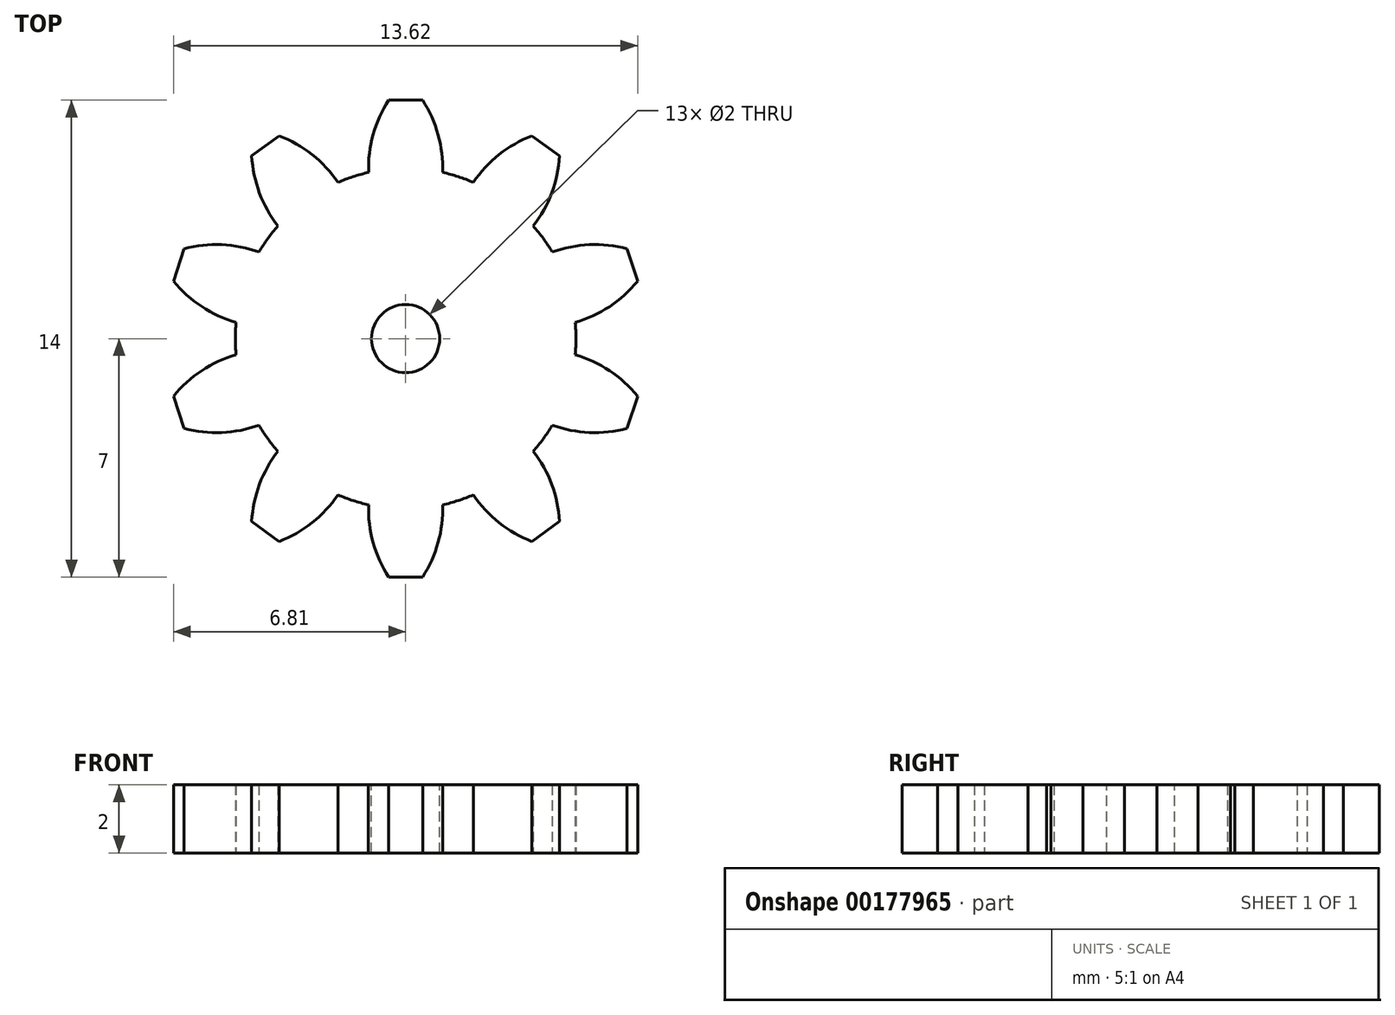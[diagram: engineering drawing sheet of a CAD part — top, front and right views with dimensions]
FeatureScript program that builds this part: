
annotation { "Feature Type Name" : "Feature", "Feature Type Description" : "" }
export const myFeature = defineFeature(function(context is Context, id is Id, definition is map)
    precondition{}
    {
        {
            var Q0;
            Q0=qCreatedBy(makeId("Top.planeOp"),FACE);
            var sketch = newSketch(context, id + "F0", { "sketchPlane" : qUnion([Q0])});
            skCircle(sketch, "E0", {"center": v(0, 0) * mm, "radius": 5 * mm});
            skLineSegment(sketch, "E1", {"start": v(0, 0) * mm, "end": v(0, 5) * mm, "construction": true});
            skLineSegment(sketch, "E2", {"start": v(0, 7) * mm, "end": v(-0.5, 7) * mm});
            skArc(sketch, "E3", {"start": v(-0.5, 7) * mm, "mid": v(-0.96, 5.98) * mm, "end": v(-1.09, 4.88) * mm});
            skLineSegment(sketch, "E4", {"start": v(0, 5) * mm, "end": v(0, 8.52) * mm});
            skLineSegment(sketch, "E5.MirrorCS", {"start": v(0, 7) * mm, "end": v(0.5, 7) * mm});
            skArc(sketch, "E6.MirrorCS", {"start": v(0.5, 7) * mm, "mid": v(0.96, 5.98) * mm, "end": v(1.09, 4.88) * mm});
            skArc(sketch, "E7.1.0", {"start": v(-4.52, 5.37) * mm, "mid": v(-4.3, 4.28) * mm, "end": v(-3.75, 3.3) * mm});
            skLineSegment(sketch, "E7.1.1", {"start": v(-4.11, 5.66) * mm, "end": v(-4.52, 5.37) * mm});
            skLineSegment(sketch, "E7.1.2", {"start": v(-4.11, 5.66) * mm, "end": v(-3.7, 5.96) * mm});
            skArc(sketch, "E7.1.3", {"start": v(-3.7, 5.96) * mm, "mid": v(-2.75, 5.4) * mm, "end": v(-1.99, 4.59) * mm});
            skArc(sketch, "E7.2.0", {"start": v(-6.81, 1.69) * mm, "mid": v(-5.99, 0.94) * mm, "end": v(-4.98, 0.47) * mm});
            skLineSegment(sketch, "E7.2.1", {"start": v(-6.66, 2.16) * mm, "end": v(-6.81, 1.69) * mm});
            skLineSegment(sketch, "E7.2.2", {"start": v(-6.66, 2.16) * mm, "end": v(-6.5, 2.64) * mm});
            skArc(sketch, "E7.2.3", {"start": v(-6.5, 2.64) * mm, "mid": v(-5.4, 2.76) * mm, "end": v(-4.3, 2.54) * mm});
            skArc(sketch, "E7.3.0", {"start": v(-6.5, -2.64) * mm, "mid": v(-5.4, -2.76) * mm, "end": v(-4.3, -2.54) * mm});
            skLineSegment(sketch, "E7.3.1", {"start": v(-6.66, -2.16) * mm, "end": v(-6.5, -2.64) * mm});
            skLineSegment(sketch, "E7.3.2", {"start": v(-6.66, -2.16) * mm, "end": v(-6.81, -1.69) * mm});
            skArc(sketch, "E7.3.3", {"start": v(-6.81, -1.69) * mm, "mid": v(-5.99, -0.94) * mm, "end": v(-4.98, -0.47) * mm});
            skArc(sketch, "E7.4.0", {"start": v(-3.7, -5.96) * mm, "mid": v(-2.75, -5.4) * mm, "end": v(-1.99, -4.59) * mm});
            skLineSegment(sketch, "E7.4.1", {"start": v(-4.11, -5.66) * mm, "end": v(-3.7, -5.96) * mm});
            skLineSegment(sketch, "E7.4.2", {"start": v(-4.11, -5.66) * mm, "end": v(-4.52, -5.37) * mm});
            skArc(sketch, "E7.4.3", {"start": v(-4.52, -5.37) * mm, "mid": v(-4.3, -4.28) * mm, "end": v(-3.75, -3.3) * mm});
            skArc(sketch, "E7.5.0", {"start": v(0.5, -7) * mm, "mid": v(0.96, -5.98) * mm, "end": v(1.09, -4.88) * mm});
            skLineSegment(sketch, "E7.5.1", {"start": v(0, -7) * mm, "end": v(0.5, -7) * mm});
            skLineSegment(sketch, "E7.5.2", {"start": v(0, -7) * mm, "end": v(-0.5, -7) * mm});
            skArc(sketch, "E7.5.3", {"start": v(-0.5, -7) * mm, "mid": v(-0.96, -5.98) * mm, "end": v(-1.09, -4.88) * mm});
            skArc(sketch, "E7.6.0", {"start": v(4.52, -5.37) * mm, "mid": v(4.3, -4.28) * mm, "end": v(3.75, -3.3) * mm});
            skLineSegment(sketch, "E7.6.1", {"start": v(4.11, -5.66) * mm, "end": v(4.52, -5.37) * mm});
            skLineSegment(sketch, "E7.6.2", {"start": v(4.11, -5.66) * mm, "end": v(3.7, -5.96) * mm});
            skArc(sketch, "E7.6.3", {"start": v(3.7, -5.96) * mm, "mid": v(2.75, -5.4) * mm, "end": v(1.99, -4.59) * mm});
            skArc(sketch, "E7.7.0", {"start": v(6.81, -1.69) * mm, "mid": v(5.99, -0.94) * mm, "end": v(4.98, -0.47) * mm});
            skLineSegment(sketch, "E7.7.1", {"start": v(6.66, -2.16) * mm, "end": v(6.81, -1.69) * mm});
            skLineSegment(sketch, "E7.7.2", {"start": v(6.66, -2.16) * mm, "end": v(6.5, -2.64) * mm});
            skArc(sketch, "E7.7.3", {"start": v(6.5, -2.64) * mm, "mid": v(5.4, -2.76) * mm, "end": v(4.3, -2.54) * mm});
            skArc(sketch, "E7.8.0", {"start": v(6.5, 2.64) * mm, "mid": v(5.4, 2.76) * mm, "end": v(4.3, 2.54) * mm});
            skLineSegment(sketch, "E7.8.1", {"start": v(6.66, 2.16) * mm, "end": v(6.5, 2.64) * mm});
            skLineSegment(sketch, "E7.8.2", {"start": v(6.66, 2.16) * mm, "end": v(6.81, 1.69) * mm});
            skArc(sketch, "E7.8.3", {"start": v(6.81, 1.69) * mm, "mid": v(5.99, 0.94) * mm, "end": v(4.98, 0.47) * mm});
            skArc(sketch, "E7.9.0", {"start": v(3.7, 5.96) * mm, "mid": v(2.75, 5.4) * mm, "end": v(1.99, 4.59) * mm});
            skLineSegment(sketch, "E7.9.1", {"start": v(4.11, 5.66) * mm, "end": v(3.7, 5.96) * mm});
            skLineSegment(sketch, "E7.9.2", {"start": v(4.11, 5.66) * mm, "end": v(4.52, 5.37) * mm});
            skArc(sketch, "E7.9.3", {"start": v(4.52, 5.37) * mm, "mid": v(4.3, 4.28) * mm, "end": v(3.75, 3.3) * mm});
            skSolve(sketch);
        }
        {
            var Q0;
            Q0=qSketchRegion(id+"F0",true);
            extrude(context, id + "F1", {"entities" : qUnion([Q0]), "depth" : 2 * mm});
        }
        {
            var Q0;
            Q0=makeQuery(id+"F1.opExtrude","CAP_FACE",FACE,{"disambiguationData":[OSD([sQuery(id+"F0.wireOp",EDGE,"E0"),sQuery(id+"F0.wireOp",EDGE,"E2"),sQuery(id+"F0.wireOp",EDGE,"E3"),sQuery(id+"F0.wireOp",EDGE,"E5.MirrorCS"),sQuery(id+"F0.wireOp",EDGE,"E6.MirrorCS"),sQuery(id+"F0.wireOp",EDGE,"E7.1.0"),sQuery(id+"F0.wireOp",EDGE,"E7.1.1"),sQuery(id+"F0.wireOp",EDGE,"E7.1.2"),sQuery(id+"F0.wireOp",EDGE,"E7.1.3"),sQuery(id+"F0.wireOp",EDGE,"E7.2.0"),sQuery(id+"F0.wireOp",EDGE,"E7.2.1"),sQuery(id+"F0.wireOp",EDGE,"E7.2.2"),sQuery(id+"F0.wireOp",EDGE,"E7.2.3"),sQuery(id+"F0.wireOp",EDGE,"E7.3.0"),sQuery(id+"F0.wireOp",EDGE,"E7.3.1"),sQuery(id+"F0.wireOp",EDGE,"E7.3.2"),sQuery(id+"F0.wireOp",EDGE,"E7.3.3"),sQuery(id+"F0.wireOp",EDGE,"E7.4.0"),sQuery(id+"F0.wireOp",EDGE,"E7.4.1"),sQuery(id+"F0.wireOp",EDGE,"E7.4.2"),sQuery(id+"F0.wireOp",EDGE,"E7.4.3"),sQuery(id+"F0.wireOp",EDGE,"E7.5.0"),sQuery(id+"F0.wireOp",EDGE,"E7.5.1"),sQuery(id+"F0.wireOp",EDGE,"E7.5.2"),sQuery(id+"F0.wireOp",EDGE,"E7.5.3"),sQuery(id+"F0.wireOp",EDGE,"E7.6.0"),sQuery(id+"F0.wireOp",EDGE,"E7.6.1"),sQuery(id+"F0.wireOp",EDGE,"E7.6.2"),sQuery(id+"F0.wireOp",EDGE,"E7.6.3"),sQuery(id+"F0.wireOp",EDGE,"E7.7.0"),sQuery(id+"F0.wireOp",EDGE,"E7.7.1"),sQuery(id+"F0.wireOp",EDGE,"E7.7.2"),sQuery(id+"F0.wireOp",EDGE,"E7.7.3"),sQuery(id+"F0.wireOp",EDGE,"E7.8.0"),sQuery(id+"F0.wireOp",EDGE,"E7.8.1"),sQuery(id+"F0.wireOp",EDGE,"E7.8.2"),sQuery(id+"F0.wireOp",EDGE,"E7.8.3"),sQuery(id+"F0.wireOp",EDGE,"E7.9.0"),sQuery(id+"F0.wireOp",EDGE,"E7.9.1"),sQuery(id+"F0.wireOp",EDGE,"E7.9.2"),sQuery(id+"F0.wireOp",EDGE,"E7.9.3"),sQuery(id+"F0.wireOp",EDGE,"E7.10.0"),sQuery(id+"F0.wireOp",EDGE,"E7.10.1"),sQuery(id+"F0.wireOp",EDGE,"E7.10.2"),sQuery(id+"F0.wireOp",EDGE,"E7.10.3"),sQuery(id+"F0.wireOp",EDGE,"E7.11.0"),sQuery(id+"F0.wireOp",EDGE,"E7.11.1"),sQuery(id+"F0.wireOp",EDGE,"E7.11.2"),sQuery(id+"F0.wireOp",EDGE,"E7.11.3"),sQuery(id+"F0.wireOp",EDGE,"E7.12.0"),sQuery(id+"F0.wireOp",EDGE,"E7.12.1"),sQuery(id+"F0.wireOp",EDGE,"E7.12.2"),sQuery(id+"F0.wireOp",EDGE,"E7.12.3"),sQuery(id+"F0.wireOp",EDGE,"E7.13.0"),sQuery(id+"F0.wireOp",EDGE,"E7.13.1"),sQuery(id+"F0.wireOp",EDGE,"E7.13.2"),sQuery(id+"F0.wireOp",EDGE,"E7.13.3"),sQuery(id+"F0.wireOp",EDGE,"E7.14.0"),sQuery(id+"F0.wireOp",EDGE,"E7.14.1"),sQuery(id+"F0.wireOp",EDGE,"E7.14.2"),sQuery(id+"F0.wireOp",EDGE,"E7.14.3"),sQuery(id+"F0.wireOp",EDGE,"E7.15.0"),sQuery(id+"F0.wireOp",EDGE,"E7.15.1"),sQuery(id+"F0.wireOp",EDGE,"E7.15.2"),sQuery(id+"F0.wireOp",EDGE,"E7.15.3")])],"isStart":false});
            var sketch = newSketch(context, id + "F2", { "sketchPlane" : qUnion([Q0])});
            skCircle(sketch, "E8", {"center": v(0, 0) * mm, "radius": 1 * mm});
            skSolve(sketch);
        }
        {
            var Q0;
            Q0=qSketchRegion(id+"F2",true);
            extrude(context, id + "F3", {"entities" : qUnion([Q0]), "operationType" : NewBodyOperationType.REMOVE, "endBound" : BoundingType.THROUGH_ALL, "oppositeDirection" : true, "depth" : 25 * mm});
        }
    });
